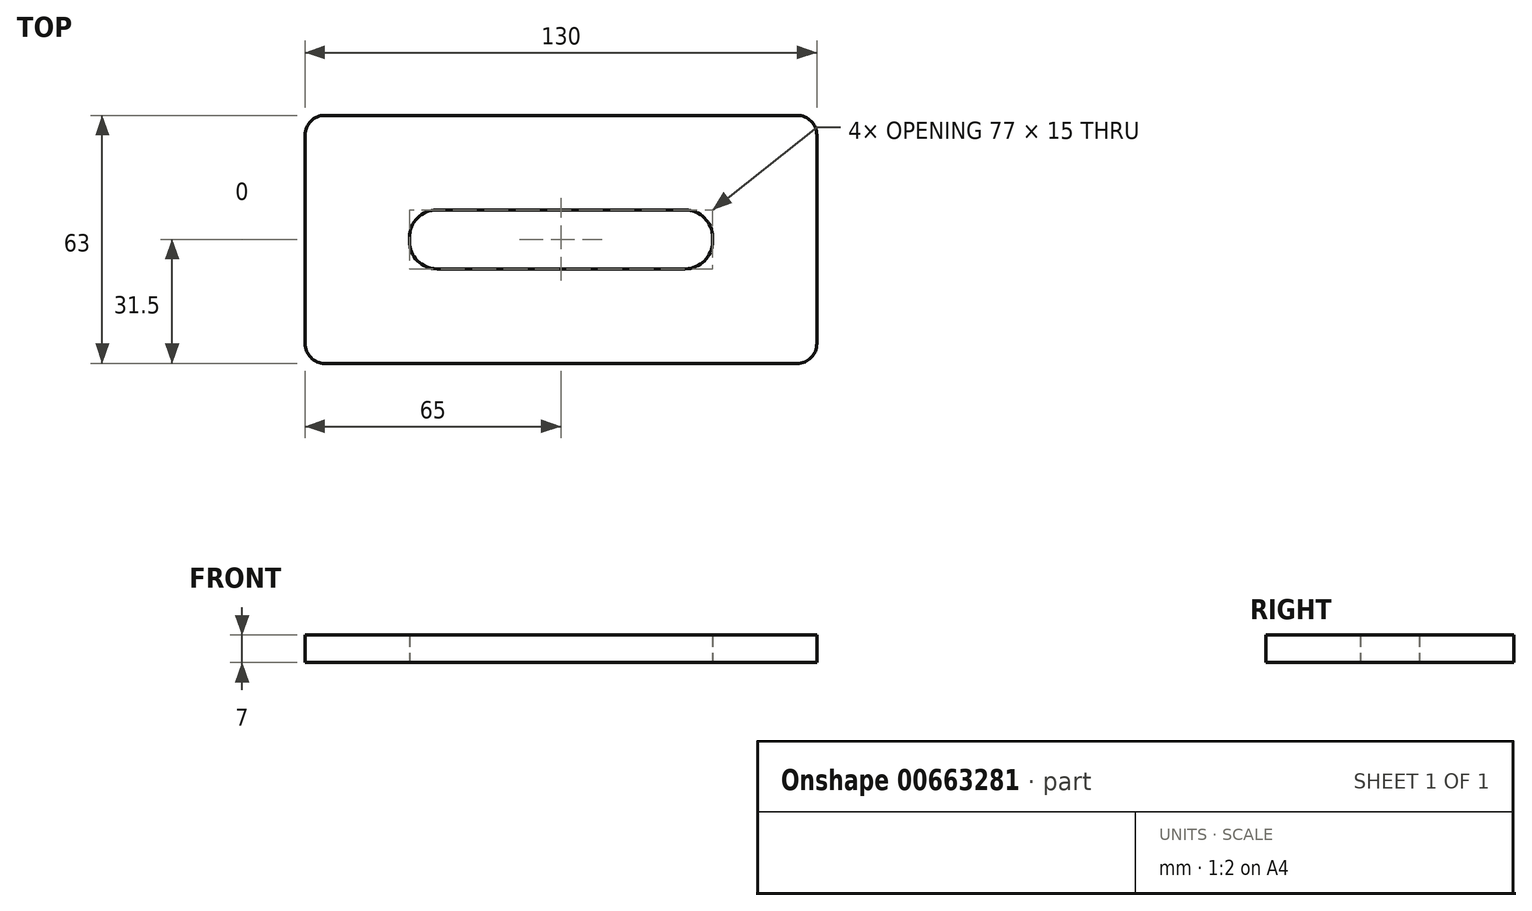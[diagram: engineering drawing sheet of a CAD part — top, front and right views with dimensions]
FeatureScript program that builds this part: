
annotation { "Feature Type Name" : "Feature", "Feature Type Description" : "" }
export const myFeature = defineFeature(function(context is Context, id is Id, definition is map)
    precondition{}
    {
        {
            var Q0;
            Q0=qCreatedBy(makeId("Top.planeOp"),FACE);
            var sketch = newSketch(context, id + "F0", { "sketchPlane" : qUnion([Q0])});
            skLineSegment(sketch, "E0.bottom", {"start": v(60, 31.5) * mm, "end": v(-60, 31.5) * mm});
            skLineSegment(sketch, "E0.top", {"start": v(60, -31.5) * mm, "end": v(-60, -31.5) * mm});
            skLineSegment(sketch, "E0.left", {"start": v(65, 26.5) * mm, "end": v(65, -26.5) * mm});
            skLineSegment(sketch, "E0.right", {"start": v(-65, 26.5) * mm, "end": v(-65, -26.5) * mm});
            skPoint(sketch, "E0.middle", {"position": v(0, 0) * mm});
            skLineSegment(sketch, "E1.bottom", {"start": v(31.5, 7.5) * mm, "end": v(-31.5, 7.5) * mm});
            skLineSegment(sketch, "E1.top", {"start": v(31.5, -7.5) * mm, "end": v(-31.5, -7.5) * mm});
            skLineSegment(sketch, "E1.left", {"start": v(38.5, 0.5) * mm, "end": v(38.5, -0.5) * mm});
            skLineSegment(sketch, "E1.right", {"start": v(-38.5, 0.5) * mm, "end": v(-38.5, -0.5) * mm});
            skPoint(sketch, "E2.visualSharp", {"position": v(-38.5, 7.5) * mm});
            skArc(sketch, "E2.filletArc", {"start": v(-31.5, 7.5) * mm, "mid": v(-36.45, 5.45) * mm, "end": v(-38.5, 0.5) * mm});
            skPoint(sketch, "E3.visualSharp", {"position": v(-38.5, -7.5) * mm});
            skArc(sketch, "E3.filletArc", {"start": v(-38.5, -0.5) * mm, "mid": v(-36.45, -5.45) * mm, "end": v(-31.5, -7.5) * mm});
            skPoint(sketch, "E4.visualSharp", {"position": v(38.5, 7.5) * mm});
            skArc(sketch, "E4.filletArc", {"start": v(38.5, 0.5) * mm, "mid": v(36.45, 5.45) * mm, "end": v(31.5, 7.5) * mm});
            skPoint(sketch, "E5.visualSharp", {"position": v(38.5, -7.5) * mm});
            skArc(sketch, "E5.filletArc", {"start": v(31.5, -7.5) * mm, "mid": v(36.45, -5.45) * mm, "end": v(38.5, -0.5) * mm});
            skPoint(sketch, "E6.visualSharp", {"position": v(-65, 31.5) * mm});
            skArc(sketch, "E6.filletArc", {"start": v(-60, 31.5) * mm, "mid": v(-63.54, 30.04) * mm, "end": v(-65, 26.5) * mm});
            skPoint(sketch, "E7.visualSharp", {"position": v(-65, -31.5) * mm});
            skArc(sketch, "E7.filletArc", {"start": v(-65, -26.5) * mm, "mid": v(-63.54, -30.04) * mm, "end": v(-60, -31.5) * mm});
            skPoint(sketch, "E8.visualSharp", {"position": v(65, 31.5) * mm});
            skArc(sketch, "E8.filletArc", {"start": v(65, 26.5) * mm, "mid": v(63.54, 30.04) * mm, "end": v(60, 31.5) * mm});
            skPoint(sketch, "E9.visualSharp", {"position": v(65, -31.5) * mm});
            skArc(sketch, "E9.filletArc", {"start": v(60, -31.5) * mm, "mid": v(63.54, -30.04) * mm, "end": v(65, -26.5) * mm});
            skSolve(sketch);
        }
        {
            var Q0;
            Q0=makeQuery(id+"F0.imprint","IMPRINT",FACE,{"disambiguationData":[TD([[makeQuery(id+"F0.imprint","IMPRINT",EDGE,{"derivedFrom":sQuery(id+"F0.wireOp",EDGE,"E0.bottom")}),1.0]])]});
            extrude(context, id + "F1", {"entities" : qUnion([Q0]), "depth" : 7 * mm, "offsetDistance" : 25 * mm});
        }
    });
